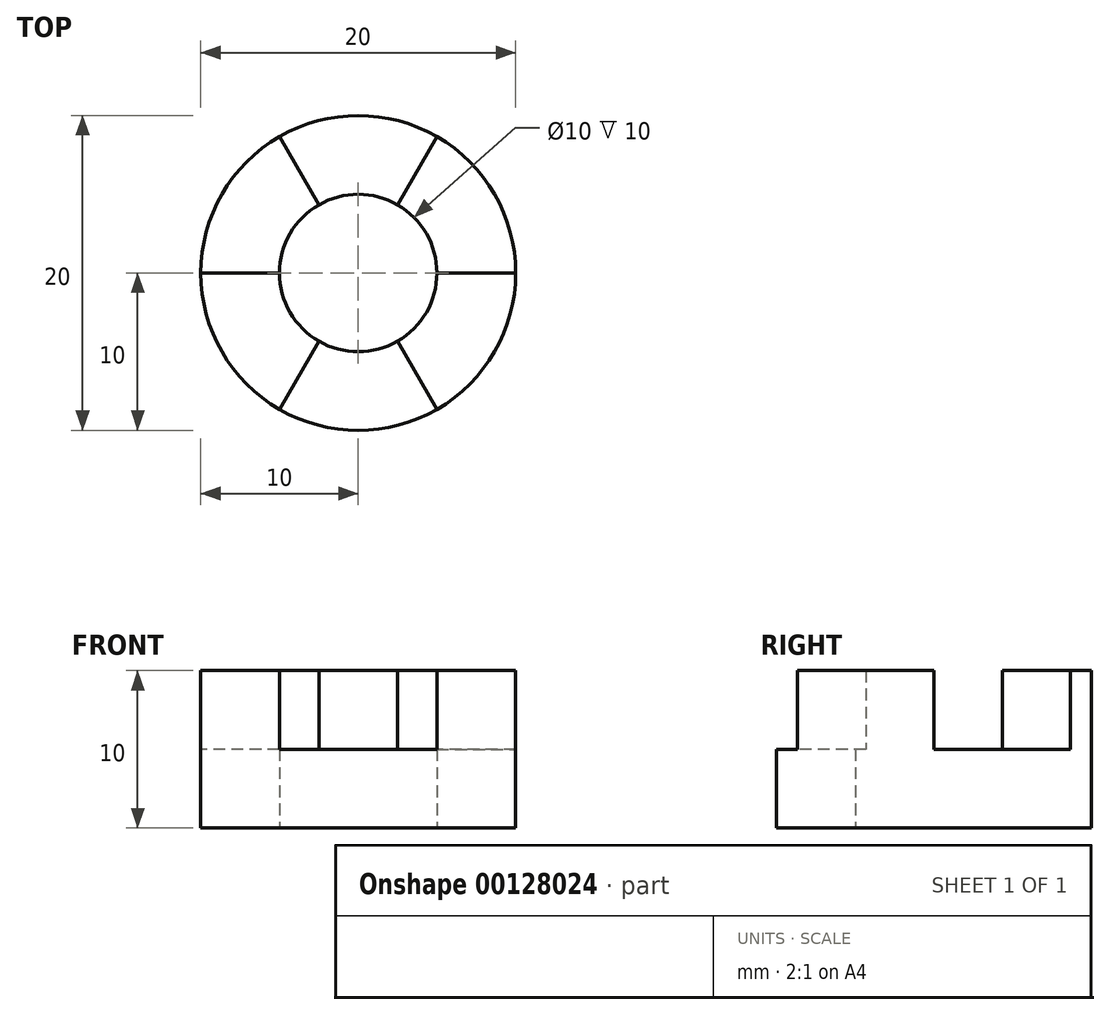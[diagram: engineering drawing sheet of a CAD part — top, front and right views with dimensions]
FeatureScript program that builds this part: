
annotation { "Feature Type Name" : "Feature", "Feature Type Description" : "" }
export const myFeature = defineFeature(function(context is Context, id is Id, definition is map)
    precondition{}
    {
        {
            var Q0;
            Q0=qCreatedBy(makeId("Top.planeOp"),FACE);
            var sketch = newSketch(context, id + "F0", { "sketchPlane" : qUnion([Q0])});
            skCircle(sketch, "E0", {"center": v(0, 0) * mm, "radius": 5 * mm});
            skCircle(sketch, "E1", {"center": v(0, 0) * mm, "radius": 10 * mm});
            skSolve(sketch);
        }
        {
            var Q0;
            Q0 = qSketchRegion(id + "F0", true);
            extrude(context, id + "F1", {"entities" : qUnion([Q0]), "depth" : 5 * mm});
        }
        {
            var Q0;
            Q0=makeQuery(id+"F1.opExtrude","CAP_FACE",FACE,{"disambiguationData":[OSD([sQuery(id+"F0.wireOp",EDGE,"E0"),sQuery(id+"F0.wireOp",EDGE,"E1")])],"isStart":false});
            var sketch = newSketch(context, id + "F2", { "sketchPlane" : qUnion([Q0])});
            skLineSegment(sketch, "E2", {"start": v(0, 0) * mm, "end": v(0, 10) * mm, "construction": true});
            skLineSegment(sketch, "E3", {"start": v(0, 0) * mm, "end": v(-8.66, -5) * mm, "construction": true});
            skLineSegment(sketch, "E4", {"start": v(0, 0) * mm, "end": v(8.66, -5) * mm, "construction": true});
            skLineSegment(sketch, "E5", {"start": v(-5, 0) * mm, "end": v(-10, 0) * mm});
            skLineSegment(sketch, "E6", {"start": v(-2.5, -4.33) * mm, "end": v(-5, -8.66) * mm});
            skArc(sketch, "E7", {"start": v(-5, 0) * mm, "mid": v(-4.33, -2.5) * mm, "end": v(-2.5, -4.33) * mm});
            skArc(sketch, "E8", {"start": v(-10, 0) * mm, "mid": v(-8.66, -5) * mm, "end": v(-5, -8.66) * mm});
            skLineSegment(sketch, "E9.1.0", {"start": v(2.5, -4.33) * mm, "end": v(5, -8.66) * mm});
            skArc(sketch, "E9.1.1", {"start": v(2.5, -4.33) * mm, "mid": v(4.33, -2.5) * mm, "end": v(5, 0) * mm});
            skLineSegment(sketch, "E9.1.2", {"start": v(5, 0) * mm, "end": v(10, 0) * mm});
            skArc(sketch, "E9.1.3", {"start": v(5, -8.66) * mm, "mid": v(8.66, -5) * mm, "end": v(10, 0) * mm});
            skLineSegment(sketch, "E9.2.0", {"start": v(2.5, 4.33) * mm, "end": v(5, 8.66) * mm});
            skArc(sketch, "E9.2.1", {"start": v(2.5, 4.33) * mm, "mid": v(0, 5) * mm, "end": v(-2.5, 4.33) * mm});
            skLineSegment(sketch, "E9.2.2", {"start": v(-2.5, 4.33) * mm, "end": v(-5, 8.66) * mm});
            skArc(sketch, "E9.2.3", {"start": v(5, 8.66) * mm, "mid": v(0, 10) * mm, "end": v(-5, 8.66) * mm});
            skSolve(sketch);
        }
        {
            var Q0;
            Q0 = qSketchRegion(id + "F2", true);
            extrude(context, id + "F3", {"entities" : qUnion([Q0]), "operationType" : NewBodyOperationType.ADD, "depth" : 5 * mm});
        }
    });
